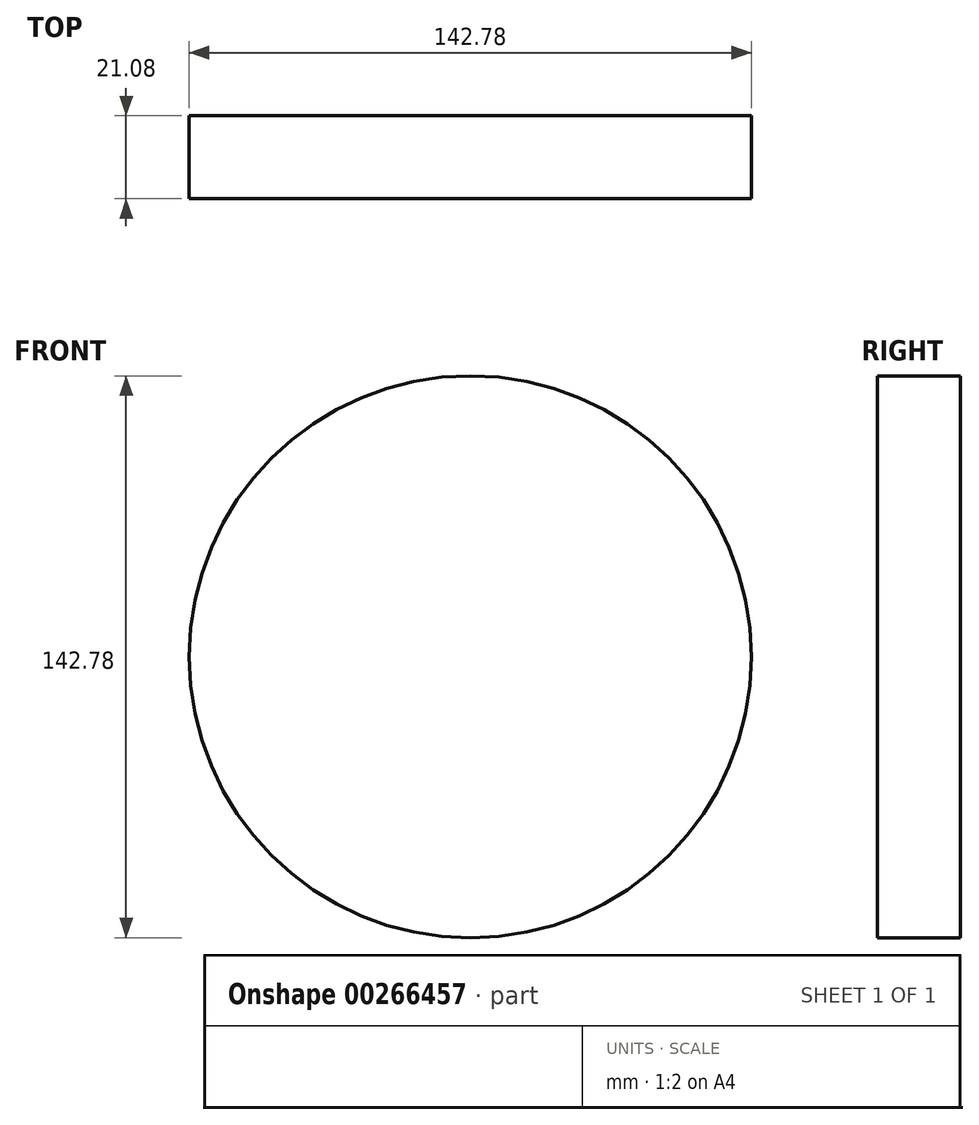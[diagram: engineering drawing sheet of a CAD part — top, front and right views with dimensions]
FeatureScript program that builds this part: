
annotation { "Feature Type Name" : "Feature", "Feature Type Description" : "" }
export const myFeature = defineFeature(function(context is Context, id is Id, definition is map)
    precondition{}
    {
        {
            var Q0;
            Q0=qCreatedBy(makeId("Front.planeOp"),FACE);
            var sketch = newSketch(context, id + "F0", { "sketchPlane" : qUnion([Q0])});
            skCircle(sketch, "E0", {"center": v(-51.49, 27.91) * mm, "radius": 71.4 * mm});
            skSolve(sketch);
        }
        {
            var Q0;
            Q0=makeQuery(id+"F0.imprint","IMPRINT",FACE,{"disambiguationData":[TD([[makeQuery(id+"F0.imprint","IMPRINT",EDGE,{"derivedFrom":sQuery(id+"F0.wireOp",EDGE,"E0")}),1.0]])]});
            extrude(context, id + "F1", {"entities" : qUnion([Q0]), "oppositeDirection" : true, "depth" : 21.08 * mm});
        }
    });
